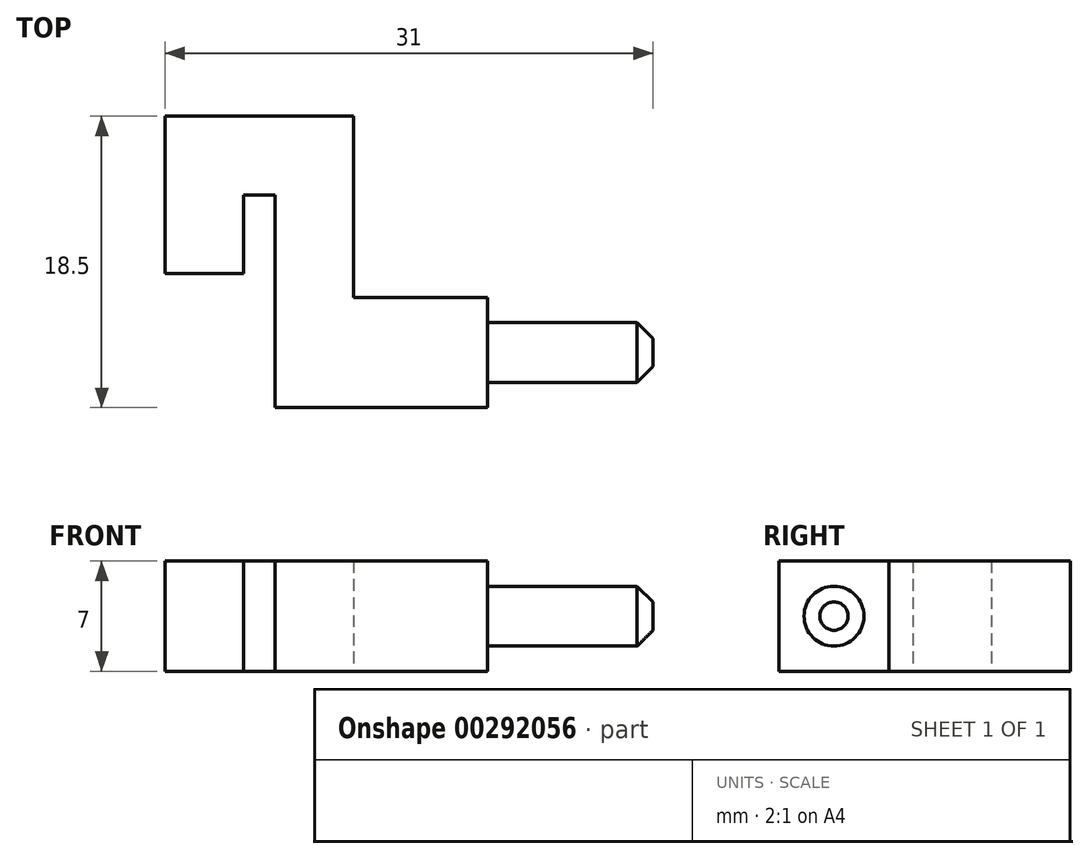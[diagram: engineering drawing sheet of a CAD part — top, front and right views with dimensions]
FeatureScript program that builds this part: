
annotation { "Feature Type Name" : "Feature", "Feature Type Description" : "" }
export const myFeature = defineFeature(function(context is Context, id is Id, definition is map)
    precondition{}
    {
        {
            var Q0;
            Q0=qCreatedBy(makeId("Top.planeOp"),FACE);
            var sketch = newSketch(context, id + "F0", { "sketchPlane" : qUnion([Q0])});
            skLineSegment(sketch, "E0", {"start": v(0, 8.5) * mm, "end": v(0, 18.5) * mm});
            skLineSegment(sketch, "E1", {"start": v(0, 18.5) * mm, "end": v(12, 18.5) * mm});
            skLineSegment(sketch, "E2", {"start": v(12, 18.5) * mm, "end": v(12, 7) * mm});
            skLineSegment(sketch, "E3", {"start": v(12, 7) * mm, "end": v(20.5, 7) * mm});
            skLineSegment(sketch, "E4", {"start": v(20.5, 7) * mm, "end": v(20.5, 0) * mm});
            skLineSegment(sketch, "E5", {"start": v(20.5, 0) * mm, "end": v(7, 0) * mm});
            skLineSegment(sketch, "E6", {"start": v(7, 0) * mm, "end": v(7, 13.5) * mm});
            skLineSegment(sketch, "E7", {"start": v(7, 13.5) * mm, "end": v(5, 13.5) * mm});
            skLineSegment(sketch, "E8", {"start": v(5, 13.5) * mm, "end": v(5, 8.5) * mm});
            skLineSegment(sketch, "E9", {"start": v(5, 8.5) * mm, "end": v(0, 8.5) * mm});
            skSolve(sketch);
        }
        {
            var Q0;
            Q0=makeQuery(id+"F0.imprint","IMPRINT",FACE,{"disambiguationData":[TD([[makeQuery(id+"F0.imprint","IMPRINT",EDGE,{"derivedFrom":sQuery(id+"F0.wireOp",EDGE,"E0")}),-1.0]])]});
            var Q1;
            Q1=makeQuery(id+"F0.imprint","IMPRINT",FACE,{"disambiguationData":[TD([[makeQuery(id+"F0.imprint","IMPRINT",EDGE,{"derivedFrom":sQuery(id+"F0.wireOp",EDGE,"31d753be-928d-4177-8552-7aac14513e080.MirrorCS")}),1.0]])]});
            extrude(context, id + "F1", {"entities" : qUnion([Q0, Q1]), "depth" : 7 * mm});
        }
        {
            var Q0;
            Q0=makeQuery(id+"F1.opExtrude","SWEPT_FACE",FACE,{"disambiguationData":[OSD([sQuery(id+"F0.wireOp",EDGE,"E4")])]});
            var sketch = newSketch(context, id + "F2", { "sketchPlane" : qUnion([Q0])});
            skLineSegment(sketch, "E10", {"start": v(-3.44, 3.5) * mm, "end": v(9.44, 3.5) * mm, "construction": true});
            skPoint(sketch, "E10.startSnap0", {"position": v(7, 3.5) * mm});
            skPoint(sketch, "E10.endSnap0", {"position": v(7, 3.5) * mm});
            skLineSegment(sketch, "E11", {"start": v(3.5, 7) * mm, "end": v(3.5, -5.1) * mm, "construction": true});
            skPoint(sketch, "E11.endSnap0", {"position": v(3.5, 0) * mm});
            skCircle(sketch, "E12", {"center": v(3.5, 3.5) * mm, "radius": 1.9 * mm});
            skSolve(sketch);
        }
        {
            var Q0;
            Q0=makeQuery(id+"F2.imprint","IMPRINT",FACE,{"disambiguationData":[TD([[makeQuery(id+"F2.imprint","IMPRINT",EDGE,{"derivedFrom":sQuery(id+"F2.wireOp",EDGE,"E12")}),1.0]])]});
            extrude(context, id + "F3", {"entities" : qUnion([Q0]), "operationType" : NewBodyOperationType.ADD, "depth" : 10.5 * mm});
        }
        {
            var Q0;
            Q0=makeQuery(id+"F3.opExtrude","CAP_EDGE",EDGE,{"disambiguationData":[OSD([sQuery(id+"F2.wireOp",EDGE,"E12")])],"isStart":false});
            chamfer(context, id + "F4", {"entities" : qUnion([Q0]), "width" : 1 * mm, "tangentPropagation" : true});
        }
    });
